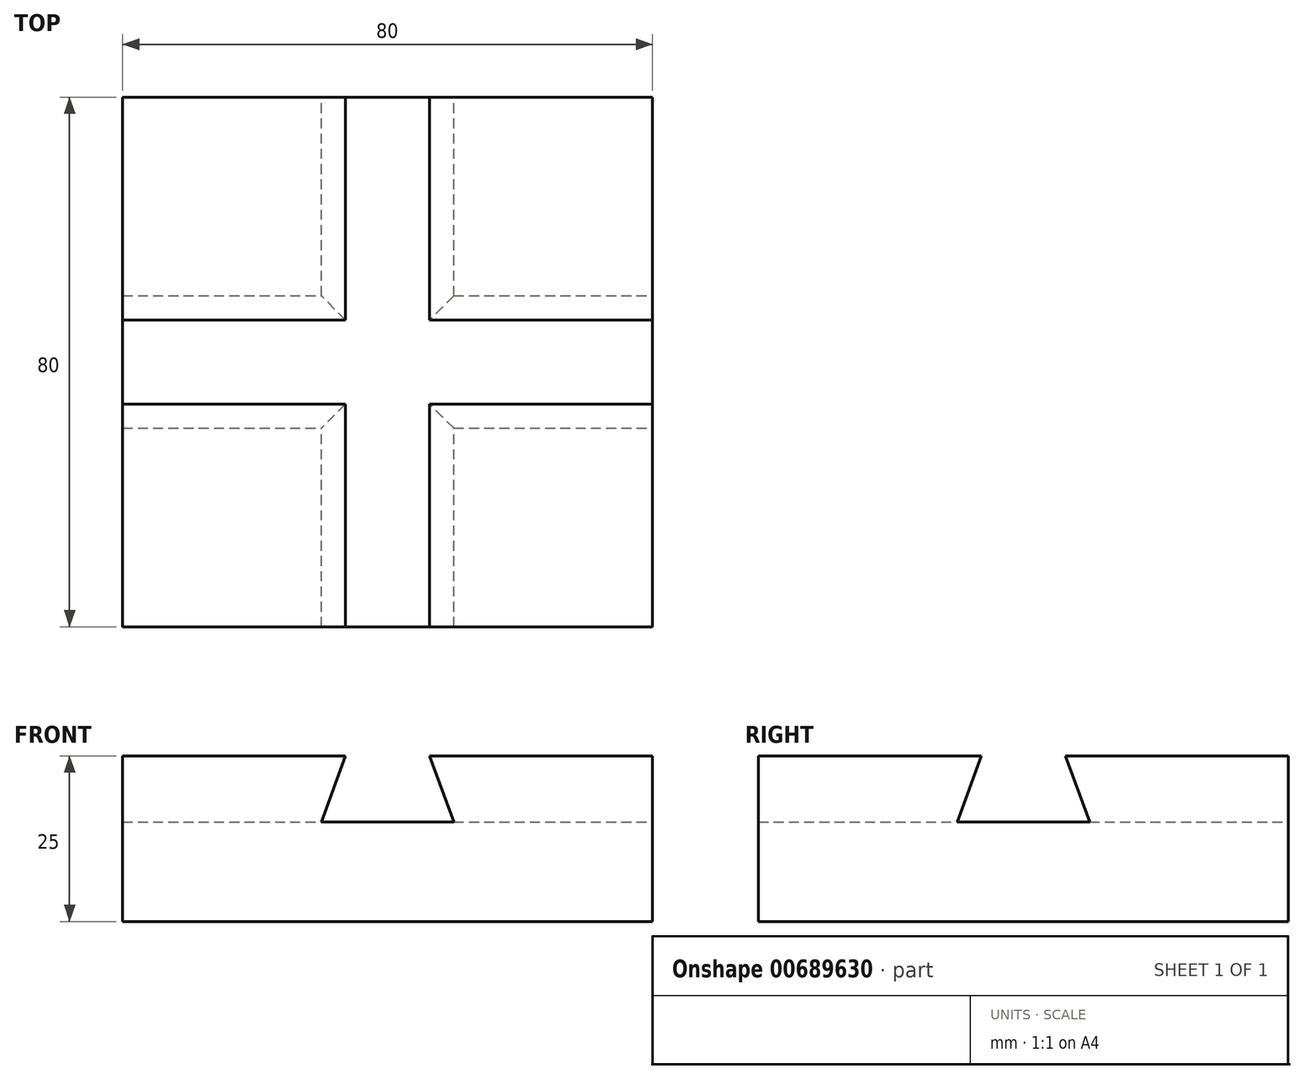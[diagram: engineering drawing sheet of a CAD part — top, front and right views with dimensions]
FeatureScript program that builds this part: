
annotation { "Feature Type Name" : "Feature", "Feature Type Description" : "" }
export const myFeature = defineFeature(function(context is Context, id is Id, definition is map)
    precondition{}
    {
        {
            var Q0;
            Q0=qCreatedBy(makeId("Front.planeOp"),FACE);
            var sketch = newSketch(context, id + "F0", { "sketchPlane" : qUnion([Q0])});
            skLineSegment(sketch, "E0.bottom", {"start": v(0, 0) * mm, "end": v(-80, 0) * mm});
            skLineSegment(sketch, "E0.left", {"start": v(0, 0) * mm, "end": v(0, 25) * mm});
            skLineSegment(sketch, "E0.right", {"start": v(-80, 0) * mm, "end": v(-80, 25) * mm});
            skLineSegment(sketch, "E1", {"start": v(-80, 25) * mm, "end": v(-46.36, 25) * mm});
            skLineSegment(sketch, "E2", {"start": v(0, 25) * mm, "end": v(-33.64, 25) * mm});
            skLineSegment(sketch, "E3", {"start": v(-33.64, 25) * mm, "end": v(-30, 15) * mm});
            skLineSegment(sketch, "E4", {"start": v(-30, 15) * mm, "end": v(-50, 15) * mm});
            skLineSegment(sketch, "E5", {"start": v(-50, 15) * mm, "end": v(-46.36, 25) * mm});
            skPoint(sketch, "E6.endSnap0", {"position": v(-40, 25) * mm});
            skLineSegment(sketch, "E7.trimOffspring", {"start": v(-46.36, 25) * mm, "end": v(-80, 25) * mm});
            skSolve(sketch);
        }
        {
            var Q0;
            Q0=makeQuery(id+"F0.imprint","IMPRINT",FACE,{"disambiguationData":[TD([[makeQuery(id+"F0.imprint","IMPRINT",EDGE,{"derivedFrom":sQuery(id+"F0.wireOp",EDGE,"E0.bottom")}),-1.0]])]});
            extrude(context, id + "F1", {"entities" : qUnion([Q0]), "depth" : 80 * mm, "offsetDistance" : 25 * mm});
        }
        {
            var Q0;
            Q0=makeQuery(id+"F1.opExtrude","SWEPT_FACE",FACE,{"disambiguationData":[OSD([sQuery(id+"F0.wireOp",EDGE,"E0.left")])]});
            var sketch = newSketch(context, id + "F2", { "sketchPlane" : qUnion([Q0])});
            skLineSegment(sketch, "E8.bottom", {"start": v(-30, 15) * mm, "end": v(-50, 15) * mm});
            skPoint(sketch, "E8.middle", {"position": v(-40, 25) * mm});
            skLineSegment(sketch, "E9", {"start": v(-50, 15) * mm, "end": v(-46.36, 25) * mm});
            skLineSegment(sketch, "E10", {"start": v(-30, 15) * mm, "end": v(-33.64, 25) * mm});
            skPoint(sketch, "E8.top.end.orphan", {"position": v(-50, 35) * mm});
            skPoint(sketch, "E8.top.start.orphan", {"position": v(-30, 35) * mm});
            skSolve(sketch);
        }
        {
            var Q0;
            Q0=makeQuery(id+"F2.imprint","IMPRINT",FACE,{"disambiguationData":[TD([[makeQuery(id+"F2.imprint","IMPRINT",EDGE,{"derivedFrom":sQuery(id+"F2.wireOp",EDGE,"E8.bottom")}),-1.0]])]});
            extrude(context, id + "F3", {"entities" : qUnion([Q0]), "operationType" : NewBodyOperationType.REMOVE, "oppositeDirection" : true, "depth" : 80 * mm, "offsetDistance" : 25 * mm});
        }
    });
